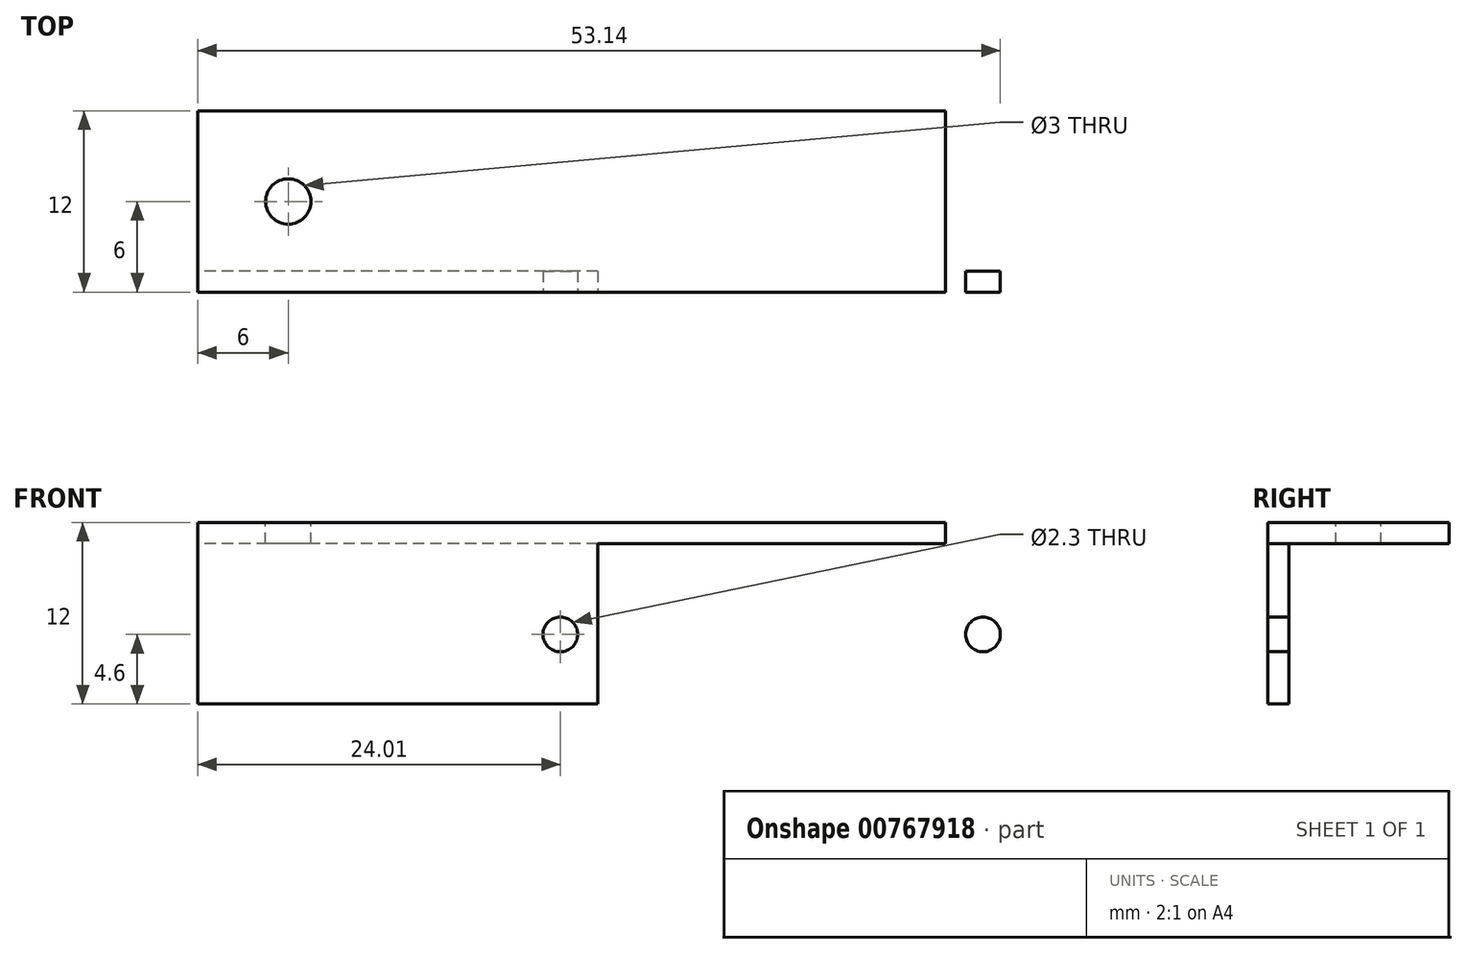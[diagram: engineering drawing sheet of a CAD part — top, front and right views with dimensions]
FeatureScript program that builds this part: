
annotation { "Feature Type Name" : "Feature", "Feature Type Description" : "" }
export const myFeature = defineFeature(function(context is Context, id is Id, definition is map)
    precondition{}
    {
        {
            var Q0;
            Q0=qCreatedBy(makeId("Right.planeOp"),FACE);
            var sketch = newSketch(context, id + "F0", { "sketchPlane" : qUnion([Q0])});
            skLineSegment(sketch, "E0", {"start": v(0, 0) * mm, "end": v(0, 12) * mm});
            skLineSegment(sketch, "E1", {"start": v(0, 12) * mm, "end": v(12, 12) * mm});
            skLineSegment(sketch, "E2.0", {"start": v(1.4, 10.6) * mm, "end": v(12, 10.6) * mm});
            skLineSegment(sketch, "E2.1", {"start": v(1.4, 0) * mm, "end": v(1.4, 10.6) * mm});
            skLineSegment(sketch, "E3", {"start": v(12, 10.6) * mm, "end": v(12, 12) * mm});
            skLineSegment(sketch, "E4", {"start": v(0, 0) * mm, "end": v(1.4, 0) * mm});
            skSolve(sketch);
        }
        {
            var Q0;
            Q0=makeQuery(id+"F0.imprint","IMPRINT",FACE,{"disambiguationData":[TD([[makeQuery(id+"F0.imprint","IMPRINT",EDGE,{"derivedFrom":sQuery(id+"F0.wireOp",EDGE,"E0")}),-1.0]])]});
            extrude(context, id + "F1", {"entities" : qUnion([Q0]), "depth" : (52 + 24) * mm, "offsetDistance" : 25 * mm});
        }
        {
            var Q0;
            Q0=makeQuery(id+"F1.opExtrude","SWEPT_FACE",FACE,{"disambiguationData":[OSD([sQuery(id+"F0.wireOp",EDGE,"E0")])]});
            var sketch = newSketch(context, id + "F2", { "sketchPlane" : qUnion([Q0])});
            skLineSegment(sketch, "E5", {"start": v(38, 12) * mm, "end": v(38, 0) * mm, "construction": true});
            skLineSegment(sketch, "E6.0", {"start": v(26.5, 12) * mm, "end": v(26.5, 0) * mm});
            skLineSegment(sketch, "E7.0", {"start": v(49.5, 12) * mm, "end": v(49.5, 0) * mm});
            skLineSegment(sketch, "E8", {"start": v(0, 10.6) * mm, "end": v(76, 10.6) * mm, "construction": true});
            skLineSegment(sketch, "E9", {"start": v(0, 4.6) * mm, "end": v(76, 4.6) * mm, "construction": true});
            skCircle(sketch, "E10", {"center": v(24, 4.6) * mm, "radius": 1.15 * mm});
            skCircle(sketch, "E11.MirrorC", {"center": v(52, 4.6) * mm, "radius": 1.15 * mm});
            skLineSegment(sketch, "E12", {"start": v(26.5, 10.6) * mm, "end": v(49.5, 10.6) * mm});
            skSolve(sketch);
        }
        {
            var Q0;
            {var subQ3=sQuery(id+"F2.wireOp",EDGE,"E12");Q0=makeQuery(id+"F2.imprint","IMPRINT",FACE,{"disambiguationData":[TD([[makeQuery(id+"F2.imprint","IMPRINT",EDGE,{"derivedFrom":subQ3}),-1.0]])]});}
            var Q1;
            Q1=makeQuery(id+"F2.imprint","IMPRINT",FACE,{"disambiguationData":[TD([[makeQuery(id+"F2.imprint","IMPRINT",EDGE,{"derivedFrom":sQuery(id+"F2.wireOp",EDGE,"E10")}),1.0]])]});
            var Q2;
            Q2=makeQuery(id+"F2.imprint","IMPRINT",FACE,{"disambiguationData":[TD([[makeQuery(id+"F2.imprint","IMPRINT",EDGE,{"derivedFrom":sQuery(id+"F2.wireOp",EDGE,"E11.MirrorC")}),-1.0]])]});
            extrude(context, id + "F3", {"entities" : qUnion([Q0, Q1, Q2]), "operationType" : NewBodyOperationType.REMOVE, "endBound" : BoundingType.UP_TO_NEXT, "oppositeDirection" : true, "depth" : 25 * mm, "offsetDistance" : 25 * mm});
        }
        {
            var Q0;
            Q0=makeQuery(id+"F1.opExtrude","SWEPT_FACE",FACE,{"disambiguationData":[OSD([sQuery(id+"F0.wireOp",EDGE,"E1")])]});
            var sketch = newSketch(context, id + "F4", { "sketchPlane" : qUnion([Q0])});
            skCircle(sketch, "E13", {"center": v(6, 6) * mm, "radius": 1.5 * mm});
            skLineSegment(sketch, "E14", {"start": v(38, 12) * mm, "end": v(38, 0) * mm, "construction": true});
            skCircle(sketch, "E15.MirrorC", {"center": v(70, 6) * mm, "radius": 1.5 * mm});
            skSolve(sketch);
        }
        {
            var Q0;
            Q0=makeQuery(id+"F4.imprint","IMPRINT",FACE,{"disambiguationData":[TD([[makeQuery(id+"F4.imprint","IMPRINT",EDGE,{"derivedFrom":sQuery(id+"F4.wireOp",EDGE,"E13")}),1.0]])]});
            var Q1;
            Q1=makeQuery(id+"F4.imprint","IMPRINT",FACE,{"disambiguationData":[TD([[makeQuery(id+"F4.imprint","IMPRINT",EDGE,{"derivedFrom":sQuery(id+"F4.wireOp",EDGE,"E15.MirrorC")}),-1.0]])]});
            extrude(context, id + "F5", {"entities" : qUnion([Q0, Q1]), "operationType" : NewBodyOperationType.REMOVE, "endBound" : BoundingType.UP_TO_NEXT, "oppositeDirection" : true, "depth" : 25 * mm, "offsetDistance" : 25 * mm});
        }
    });
